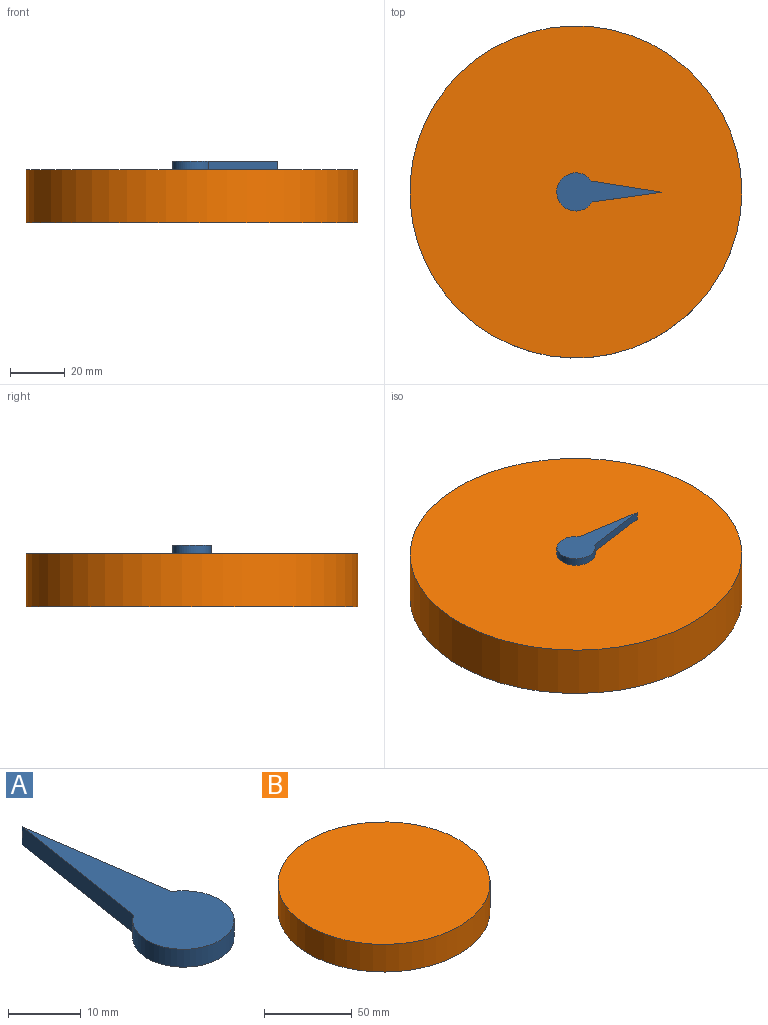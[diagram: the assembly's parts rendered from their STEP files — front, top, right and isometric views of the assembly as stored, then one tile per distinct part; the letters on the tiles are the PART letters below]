
ASSEMBLY  parts=2 mates=1
PART A: 5 faces, bbox 13.9x38.2x3 mm
  f0: cylinder r=6.95mm len=13.89mm, axis (0,0,-1), area 106.7mm2, adj f1,f2,f3,f4
  f1: plane 25.36x3.63mm, normal (0.99,0.14,0), area 76.9mm2, adj f0,f2,f3,f4
  f2: plane 25.6x4mm, normal (-0.99,0.15,0), area 77.7mm2, adj f0,f1,f3,f4
  f3: plane 38.23x13.89mm, normal (0,0,1), area 242.8mm2, adj f0,f1,f2
  f4: plane 38.23x13.89mm, normal (0,0,-1), area 242.8mm2, adj f0,f1,f2
PART B: 3 faces, bbox 120.9x120.9x19.3 mm
  f0: cylinder r=60.43mm len=120.86mm, axis (0,0,-1), area 7329.8mm2, adj f1,f2
  f1: plane 120.86x120.86mm, normal (0,0,1), area 11473.1mm2, adj f0
  f2: plane 120.86x120.86mm, normal (0,0,-1), area 11473.1mm2, adj f0
PLACE A rot(axis=(0,0,-1),90.2deg) t=(3.82,9.35,-0.32)mm
PLACE B t=(3.82,9.35,-0.32)mm fixed
MATE revolute B.f0 <-> A.f0  axis (0,0,1) through (3.82,9.35,18.98)mm
